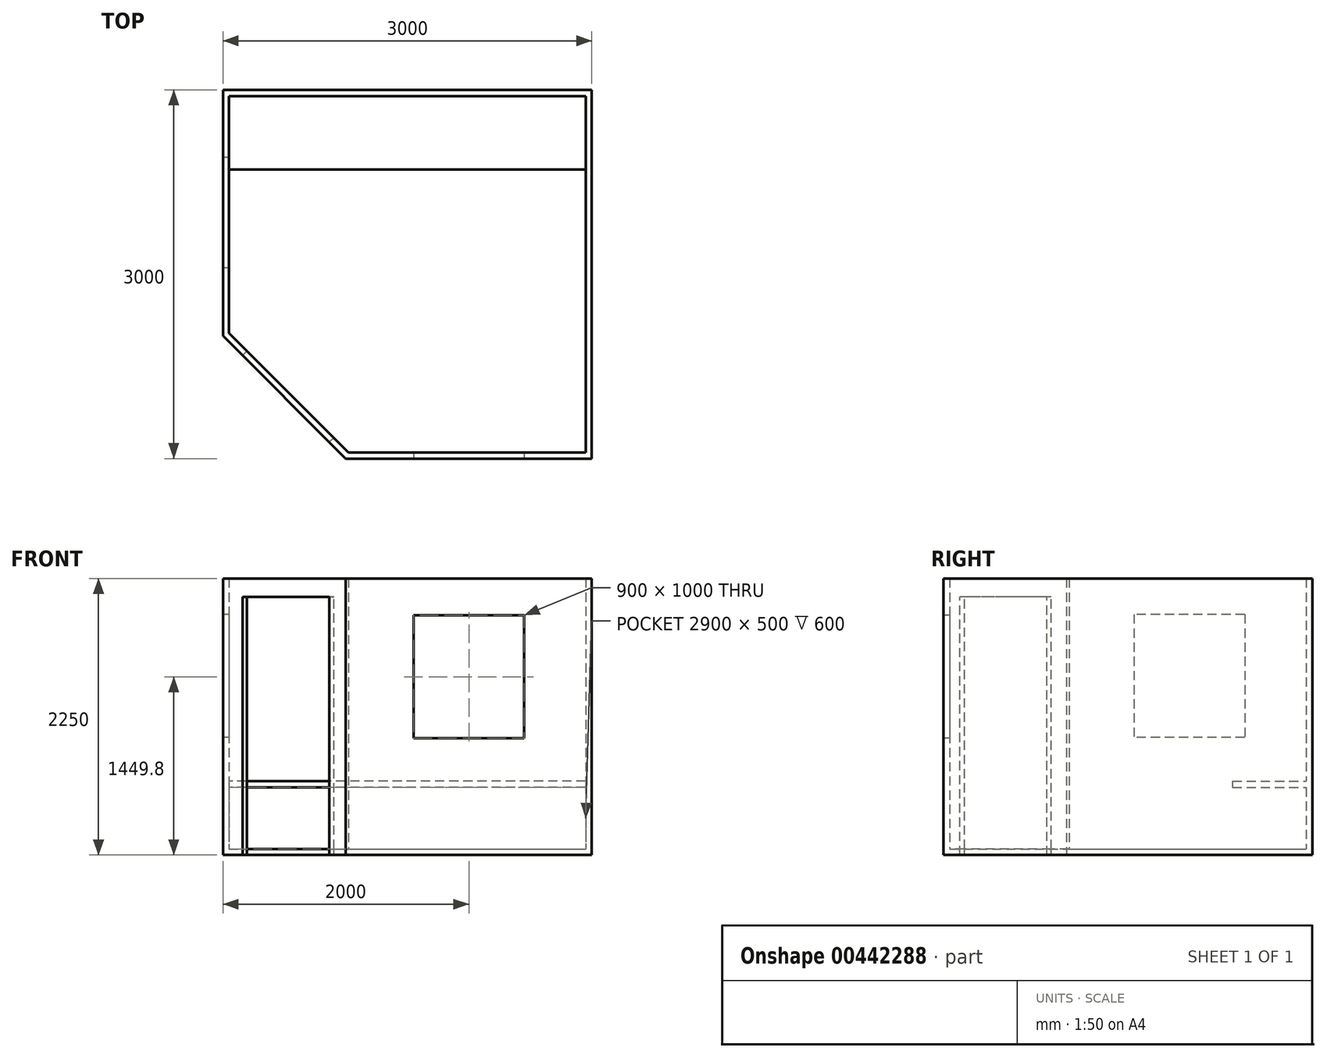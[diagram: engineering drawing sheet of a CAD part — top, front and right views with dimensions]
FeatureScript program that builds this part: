
annotation { "Feature Type Name" : "Feature", "Feature Type Description" : "" }
export const myFeature = defineFeature(function(context is Context, id is Id, definition is map)
    precondition{}
    {
        {
            var Q0;
            Q0=qCreatedBy(makeId("Top.planeOp"),FACE);
            var sketch = newSketch(context, id + "F0", { "sketchPlane" : qUnion([Q0])});
            skLineSegment(sketch, "E0.bottom", {"start": v(933.35, 66.65) * mm, "end": v(2933.35, 66.65) * mm});
            skLineSegment(sketch, "E0.top", {"start": v(-66.65, 3066.65) * mm, "end": v(2933.35, 3066.65) * mm});
            skLineSegment(sketch, "E0.left", {"start": v(-66.65, 1066.65) * mm, "end": v(-66.65, 3066.65) * mm});
            skLineSegment(sketch, "E0.right", {"start": v(2933.35, 66.65) * mm, "end": v(2933.35, 3066.65) * mm});
            skLineSegment(sketch, "E1", {"start": v(-66.65, 1066.65) * mm, "end": v(933.35, 66.65) * mm});
            skLineSegment(sketch, "E2.0", {"start": v(2883.35, 116.65) * mm, "end": v(2883.35, 3016.65) * mm});
            skLineSegment(sketch, "E2.1", {"start": v(-16.65, 3016.65) * mm, "end": v(2883.35, 3016.65) * mm});
            skLineSegment(sketch, "E2.2", {"start": v(954.06, 116.65) * mm, "end": v(2883.35, 116.65) * mm});
            skLineSegment(sketch, "E2.3", {"start": v(-16.65, 1087.36) * mm, "end": v(954.06, 116.65) * mm});
            skLineSegment(sketch, "E2.4", {"start": v(-16.65, 1087.36) * mm, "end": v(-16.65, 3016.65) * mm});
            skSolve(sketch);
        }
        {
            var Q0;
            Q0=makeQuery(id+"F0.imprint","IMPRINT",FACE,{"disambiguationData":[TD([[makeQuery(id+"F0.imprint","IMPRINT",EDGE,{"derivedFrom":sQuery(id+"F0.wireOp",EDGE,"E0.bottom")}),1.0]])]});
            extrude(context, id + "F1", {"entities" : qUnion([Q0]), "depth" : 2200 * mm});
        }
        {
            var Q0;
            Q0=makeQuery(id+"F1.opExtrude","CAP_FACE",FACE,{"disambiguationData":[OSD([sQuery(id+"F0.wireOp",EDGE,"E0.bottom"),sQuery(id+"F0.wireOp",EDGE,"E0.top"),sQuery(id+"F0.wireOp",EDGE,"E0.left"),sQuery(id+"F0.wireOp",EDGE,"E0.right"),sQuery(id+"F0.wireOp",EDGE,"E1"),sQuery(id+"F0.wireOp",EDGE,"E2.0"),sQuery(id+"F0.wireOp",EDGE,"E2.1"),sQuery(id+"F0.wireOp",EDGE,"E2.2"),sQuery(id+"F0.wireOp",EDGE,"E2.3"),sQuery(id+"F0.wireOp",EDGE,"E2.4")])],"isStart":true});
            var sketch = newSketch(context, id + "F2", { "sketchPlane" : qUnion([Q0])});
            skLineSegment(sketch, "E3", {"start": v(2933.35, -66.65) * mm, "end": v(2933.35, -3066.65) * mm});
            skLineSegment(sketch, "E4", {"start": v(2933.35, -3066.65) * mm, "end": v(-66.65, -3066.65) * mm});
            skLineSegment(sketch, "E5", {"start": v(-66.65, -3066.65) * mm, "end": v(-66.65, -1066.65) * mm});
            skLineSegment(sketch, "E6", {"start": v(-66.65, -1066.65) * mm, "end": v(933.35, -66.65) * mm});
            skLineSegment(sketch, "E7", {"start": v(933.35, -66.65) * mm, "end": v(2933.35, -66.65) * mm});
            skSolve(sketch);
        }
        {
            var Q0;
            Q0 = qSketchRegion(id + "F2", true);
            extrude(context, id + "F3", {"entities" : qUnion([Q0]), "operationType" : NewBodyOperationType.ADD, "depth" : 50 * mm});
        }
        {
            var Q0;
            Q0=makeQuery(id+"F3.boolean.opBoolean","MERGE",FACE,{"derivedFrom":[makeQuery(id+"F1.opExtrude","SWEPT_FACE",FACE,{"disambiguationData":[OSD([sQuery(id+"F0.wireOp",EDGE,"E1")])]}),makeQuery(id+"F3.opExtrude","SWEPT_FACE",FACE,{"disambiguationData":[OSD([sQuery(id+"F2.wireOp",EDGE,"E6")])]})]});
            var sketch = newSketch(context, id + "F4", { "sketchPlane" : qUnion([Q0])});
            skLineSegment(sketch, "E8.bottom", {"start": v(-576.36, -50) * mm, "end": v(423.64, -50) * mm});
            skLineSegment(sketch, "E8.top", {"start": v(-576.36, 2050) * mm, "end": v(423.64, 2050) * mm});
            skLineSegment(sketch, "E8.left", {"start": v(-576.36, -50) * mm, "end": v(-576.36, 2050) * mm});
            skLineSegment(sketch, "E8.right", {"start": v(423.64, -50) * mm, "end": v(423.64, 2050) * mm});
            skSolve(sketch);
        }
        {
            var Q0;
            Q0 = qSketchRegion(id + "F4", true);
            extrude(context, id + "F5", {"entities" : qUnion([Q0]), "operationType" : NewBodyOperationType.REMOVE, "oppositeDirection" : true, "depth" : 50 * mm});
        }
        {
            var Q0;
            Q0=makeQuery(id+"F3.boolean.opBoolean","MERGE",FACE,{"derivedFrom":[makeQuery(id+"F1.opExtrude","SWEPT_FACE",FACE,{"disambiguationData":[OSD([sQuery(id+"F0.wireOp",EDGE,"E0.bottom")])]}),makeQuery(id+"F3.opExtrude","SWEPT_FACE",FACE,{"disambiguationData":[OSD([sQuery(id+"F2.wireOp",EDGE,"E7")])]})]});
            var sketch = newSketch(context, id + "F6", { "sketchPlane" : qUnion([Q0])});
            skLineSegment(sketch, "E9.bottom", {"start": v(1483.35, 1899.8) * mm, "end": v(2383.35, 1899.8) * mm});
            skLineSegment(sketch, "E9.top", {"start": v(1483.35, 899.8) * mm, "end": v(2383.35, 899.8) * mm});
            skLineSegment(sketch, "E9.left", {"start": v(1483.35, 1899.8) * mm, "end": v(1483.35, 899.8) * mm});
            skLineSegment(sketch, "E9.right", {"start": v(2383.35, 1899.8) * mm, "end": v(2383.35, 899.8) * mm});
            skSolve(sketch);
        }
        {
            var Q0;
            Q0 = qSketchRegion(id + "F6", true);
            extrude(context, id + "F7", {"entities" : qUnion([Q0]), "operationType" : NewBodyOperationType.REMOVE, "oppositeDirection" : true, "depth" : 50 * mm});
        }
        {
            var Q0;
            Q0=makeQuery(id+"F3.boolean.opBoolean","MERGE",FACE,{"derivedFrom":[makeQuery(id+"F1.opExtrude","SWEPT_FACE",FACE,{"disambiguationData":[OSD([sQuery(id+"F0.wireOp",EDGE,"E0.left")])]}),makeQuery(id+"F3.opExtrude","SWEPT_FACE",FACE,{"disambiguationData":[OSD([sQuery(id+"F2.wireOp",EDGE,"E5")])]})]});
            var sketch = newSketch(context, id + "F8", { "sketchPlane" : qUnion([Q0])});
            skLineSegment(sketch, "E10.bottom", {"start": v(-2516.65, 1907.56) * mm, "end": v(-1616.65, 1907.56) * mm});
            skLineSegment(sketch, "E10.top", {"start": v(-2516.65, 907.56) * mm, "end": v(-1616.65, 907.56) * mm});
            skLineSegment(sketch, "E10.left", {"start": v(-2516.65, 1907.56) * mm, "end": v(-2516.65, 907.56) * mm});
            skLineSegment(sketch, "E10.right", {"start": v(-1616.65, 1907.56) * mm, "end": v(-1616.65, 907.56) * mm});
            skSolve(sketch);
        }
        {
            var Q0;
            Q0 = qSketchRegion(id + "F8", true);
            extrude(context, id + "F9", {"entities" : qUnion([Q0]), "operationType" : NewBodyOperationType.REMOVE, "oppositeDirection" : true, "depth" : 50 * mm});
        }
        {
            var Q0;
            Q0=makeQuery(id+"F1.opExtrude","SWEPT_FACE",FACE,{"disambiguationData":[OSD([sQuery(id+"F0.wireOp",EDGE,"E2.1")])]});
            var sketch = newSketch(context, id + "F10", { "sketchPlane" : qUnion([Q0])});
            skLineSegment(sketch, "E11.bottom", {"start": v(2883.35, 550) * mm, "end": v(-16.65, 550) * mm});
            skLineSegment(sketch, "E11.top", {"start": v(2883.35, 500) * mm, "end": v(-16.65, 500) * mm});
            skLineSegment(sketch, "E11.left", {"start": v(2883.35, 550) * mm, "end": v(2883.35, 500) * mm});
            skLineSegment(sketch, "E11.right", {"start": v(-16.65, 550) * mm, "end": v(-16.65, 500) * mm});
            skSolve(sketch);
        }
        {
            var Q0;
            Q0 = qSketchRegion(id + "F10", true);
            extrude(context, id + "F11", {"entities" : qUnion([Q0]), "operationType" : NewBodyOperationType.ADD, "depth" : 600 * mm});
        }
    });
